# Revit family: Facet - Ceiling Based
name_source: partatom
category: Lighting Fixtures
revit_build: Autodesk Revit Architecture 2014 (Build: 20140709_2115(x64)
units: mm (PartAtom-declared; Revit-internal decimal feet)

## types (2) — shared parameters
Apparent Load = 240 VA
ArticleNumber = See URL hyperlink
AssetType = Moveable/Fixed
BSAB 96 = SNB.2
BallastsCELMAEnergyEfficiencyIndex = Class A1/A2
CCSClassCode = UAC
CCSClassName = Belysningsarmatur
CCSTopnode = L
Color Filter = 16777215
Colour = White
ControlGearPosition = Integrated
Description = 70-80-35 General Lighting Systems
Dimming Lamp Color Temperature Shift = <None>
DocumentReference = See URL hyperlink
Documentation = See URL hyperlink
Finish = Powder coated
Frame = Riegens_Steel_Powder coated white RAL901025
Frame Depth = 64 mm
Glass Depth = 55 mm
HasProtectiveEarth = TRUE
Height 1 = 80 mm
IP_Code = IP20
IfcExportAs = IfcLightFixtureType'
IfcExportType = NOTDEFINED'
InsulationStandardClass = Class 1
InternalFuse = Only required in emergency versions
LampColourRenderingIndex = Ra>80
LampType = LED
LightFixtureMountingType = Suspended
LightFixturePlacingType = Ceiling
LightSource = LED 3000K / 4000K
LuminairePowerFactor = >0,9
Manufacturer = Riegens A/S
ManufacturerURL = www.riegens.com
Material = Steel, Lens optic from PMMA and PC.
NominalVoltage = 220-240V
Offset from ceiling = 400 mm
Optic = Direct: Prismatic optic, Indirect: Clear PC.
PhaseReference = IEC recommendations
PhotometricPerformance = In accordance with BS EN 13032-1
ProductInformation = http://riegens.com
Shape = Rectangle
Tilt Angle = 90.00°
URL = http://riegens.com
Uniclass 1.4 = JY73
Uniclass2 = Pr_70_70_49_43 Light-Emitting Diode (LED) Luminaires
Version = v.1.0

## per-type parameters (varying)
| type | BIMObjectName | Fp | Frame Width | Glass Width | LampRating | LuminaireType | Photometric Web File | Size | TotalWattage |
| Facet 49W | Facet 49W.rfa | 1300 mm | 1444 mm | 1444 mm | 49W | Suspended Direct/Indirect LED Luminaire. | Facet LED 49W DI 4000K LensC.ies | 64 x 1444 x 80 mm | Max. 54W |
| Facet 26W / 36W | Facet 26W / 36W.rfa | 1000 mm | 1164 mm | 1124 mm | 26W / 36W | Suspended Direct and Direct/Indirect LED Luminaire. | Facet LED 36W DI 4000K LensC.ies | 64 x 1164 x 80 mm | Max. 31W / 41W |

note: column(s) folded — value = type name in every type: Model, ModelReference

## geometry (parser evidence)
native form markers: Sweep x1
no freeform markers — native parametric forms only
